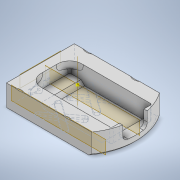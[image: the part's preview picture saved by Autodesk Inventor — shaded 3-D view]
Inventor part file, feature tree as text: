
AUTODESK INVENTOR PART (.ipt)
format: ipt  version: 2021 (Build 250183000, 183)  size: 803,328 bytes
history: native  units: in
note: dims shown in document units (in); Inventor stores cm internally (conversion verified against a paired STEP export)
features: sketch x10, extrude x8, fillet x4, chamfer x3, plane x3, mirror x2, other x1, pattern_circular x1
ambient origin geometry x8: Origin, YZ Plane, XZ Plane, XY Plane, X Axis, Y Axis, Z Axis, Center Point
bodies: Solid1 (feature_tree)
feature tree (32):
  extrude  "Extrusion1"  Depth=0.3701in TaperAngle=0.0deg
  chamfer  "Chamfer2"  Distance=0.2441in
  extrude  "Extrusion2"  Depth=0.1417in
  extrude  "Extrusion3"  Depth=0.2205in
  other  "Work Axis1"
  plane  "Work Plane1"
  extrude  "Extrusion5"  Depth=0.8268in
  extrude  "Extrusion4"  Depth=0.1969in
  fillet  "Fillet4"  Radius=0.063in
  pattern_circular  "Circular Pattern2"  [2 undecoded]
  fillet  "Fillet7"  [1 undecoded]
  extrude  "Initals"  Depth=0.0394in
  fillet  "Fillet9"  Radius=0.1181in
  fillet  "Fillet10"  Radius=0.0315in
  mirror  "Mirror6"
  sketch  "Sketch18"  dims[d18=0.2047in d19=0.0in d23=0.8268in]
  chamfer  "Chamfer4"  Distance=1.1811in
  chamfer  "Chamfer5"  Distance=0.5906in
  plane  "Work Plane5"
  extrude  "Extrusion13"  Depth=0.9728in
  mirror  "Mirror7"
  plane  "Work Plane6"
  extrude  "Extrusion14"  Depth=0.4864in
  sketch  "Sketch1"  dims[d0=2.0472in d3=0.3701in d4=0.0in]
  sketch  "Sketch2"  dims[d5=1.4315in]
  sketch  "Sketch3"  dims[d6=0.7079in]
  sketch  "Sketch4"  dims[d7=0.3539in]
  sketch  "Sketch7"  dims[d8=0.4882in d9=0.2441in d10=0.0in]
  sketch  "Sketch12"  dims[d11=0.0in d14=0.1417in]
  sketch  "Sketch13"  dims[d15=0.0in d16=0.0in d17=0.2205in]
  sketch  "Sketch19"  dims[d24=0.3539in d31=0.1969in d32=0.063in d33=0.0in]
  sketch  "Sketch20"  dims[d44=0.1417in d47=0.0in d48=0.0in d49=0.0in d51=0.0in d54=0.0394in d55=0.0in d56=45.0deg d58=0.0394in d59=0.1181in d60=1.9685in d61=240.0deg d72=0.0315in d80=1.1811in d81=0.5906in d82=0.9728in d83=0.4864in d84=0.0394in d85=0.0in d86=0.547in d87=0.2735in d88=0.0787in d89=0.0in d90=0.0787in d98=0.1024in d99=0.0in d100=0.0in d101=0.2362in d102=0.0315in d103=0.0315in d104=0.2953in d105=0.1575in d106=0.1969in d107=0.063in d108=0.0787in d109=45.0deg d110=0.063in d111=0.0787in d112=45.0deg d114=0.5906in d115=0.0in d116=0.0in d117=-0.1575in d118=0.3937in d119=0.0in d91=0.0197in d92=0.0344in d93=0.0197in d94=0.0344in d120=0.0197in d121=0.0344in d122=0.0197in d123=0.0344in]
note: 3 required parameter values undecoded (feature->parameter linkage not recoverable at this tier; creation-order binding heuristic only, values carry confidence <= 0.55)
